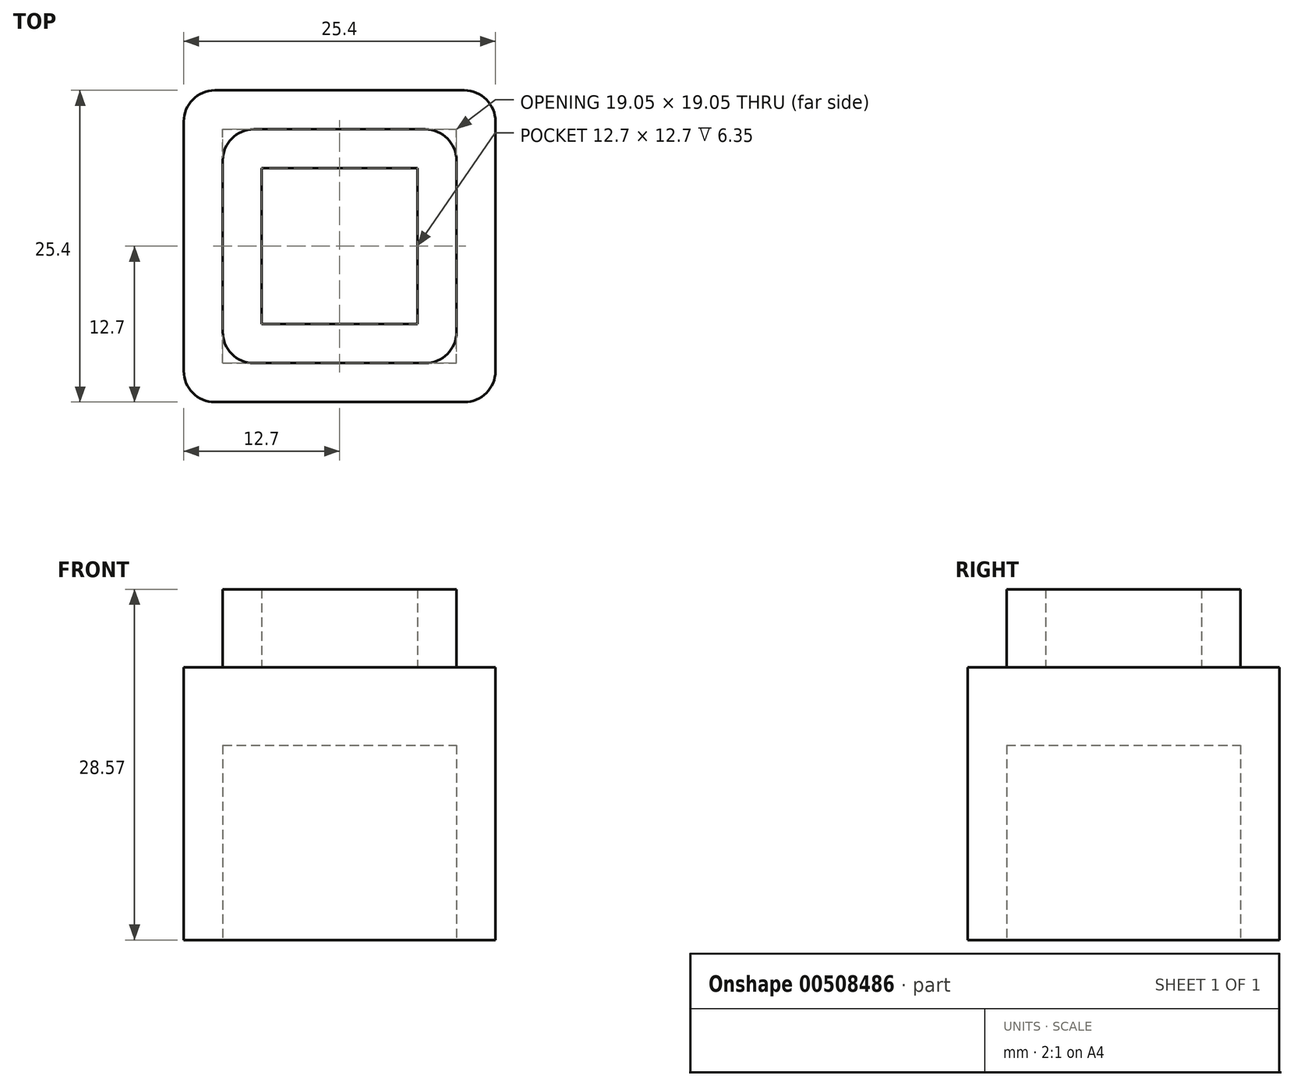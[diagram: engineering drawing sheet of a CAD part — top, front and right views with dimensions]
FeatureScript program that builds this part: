
annotation { "Feature Type Name" : "Feature", "Feature Type Description" : "" }
export const myFeature = defineFeature(function(context is Context, id is Id, definition is map)
    precondition{}
    {
        {
            var Q0;
            Q0=qCreatedBy(makeId("Top.planeOp"),FACE);
            var sketch = newSketch(context, id + "F0", { "sketchPlane" : qUnion([Q0])});
            skLineSegment(sketch, "E0.bottom", {"start": v(0, 0) * mm, "end": v(25.4, 0) * mm});
            skLineSegment(sketch, "E0.top", {"start": v(0, -25.4) * mm, "end": v(25.4, -25.4) * mm});
            skLineSegment(sketch, "E0.left", {"start": v(0, 0) * mm, "end": v(0, -25.4) * mm});
            skLineSegment(sketch, "E0.right", {"start": v(25.4, 0) * mm, "end": v(25.4, -25.4) * mm});
            skSolve(sketch);
        }
        {
            var Q0;
            Q0=qSketchRegion(id+"F0",true);
            extrude(context, id + "F1", {"entities" : qUnion([Q0]), "depth" : 22.22 * mm, "offsetDistance" : 25.4 * mm});
        }
        {
            var Q0;
            Q0=makeQuery(id+"F1.opExtrude","CAP_FACE",FACE,{"disambiguationData":[OSD([sQuery(id+"F0.wireOp",EDGE,"E0.bottom"),sQuery(id+"F0.wireOp",EDGE,"E0.top"),sQuery(id+"F0.wireOp",EDGE,"E0.left"),sQuery(id+"F0.wireOp",EDGE,"E0.right")])],"isStart":true});
            var sketch = newSketch(context, id + "F2", { "sketchPlane" : qUnion([Q0])});
            skLineSegment(sketch, "E1", {"start": v(0, 0) * mm, "end": v(25.4, 25.4) * mm, "construction": true});
            skLineSegment(sketch, "E2.bottom", {"start": v(3.18, 22.23) * mm, "end": v(22.23, 22.23) * mm});
            skLineSegment(sketch, "E2.top", {"start": v(3.18, 3.18) * mm, "end": v(22.23, 3.18) * mm});
            skLineSegment(sketch, "E2.left", {"start": v(3.18, 22.23) * mm, "end": v(3.18, 3.18) * mm});
            skLineSegment(sketch, "E2.right", {"start": v(22.23, 22.23) * mm, "end": v(22.23, 3.18) * mm});
            skLineSegment(sketch, "E3", {"start": v(3.18, 22.23) * mm, "end": v(22.23, 3.18) * mm, "construction": true});
            skPoint(sketch, "E4", {"position": v(12.7, 12.7) * mm});
            skSolve(sketch);
        }
        {
            var Q0;
            Q0=qSketchRegion(id+"F2",true);
            extrude(context, id + "F3", {"entities" : qUnion([Q0]), "operationType" : NewBodyOperationType.REMOVE, "oppositeDirection" : true, "depth" : 15.88 * mm, "offsetDistance" : 25.4 * mm});
        }
        {
            var Q0;
            Q0=makeQuery(id+"F1.opExtrude","CAP_FACE",FACE,{"disambiguationData":[OSD([sQuery(id+"F0.wireOp",EDGE,"E0.bottom"),sQuery(id+"F0.wireOp",EDGE,"E0.top"),sQuery(id+"F0.wireOp",EDGE,"E0.left"),sQuery(id+"F0.wireOp",EDGE,"E0.right")])],"isStart":false});
            var sketch = newSketch(context, id + "F4", { "sketchPlane" : qUnion([Q0])});
            skLineSegment(sketch, "E5.bottom", {"start": v(6.35, -19.05) * mm, "end": v(19.05, -19.05) * mm});
            skLineSegment(sketch, "E5.top", {"start": v(6.35, -6.35) * mm, "end": v(19.05, -6.35) * mm});
            skLineSegment(sketch, "E5.left", {"start": v(6.35, -19.05) * mm, "end": v(6.35, -6.35) * mm});
            skLineSegment(sketch, "E5.right", {"start": v(19.05, -19.05) * mm, "end": v(19.05, -6.35) * mm});
            skLineSegment(sketch, "E6.bottom", {"start": v(3.18, -22.22) * mm, "end": v(22.23, -22.22) * mm});
            skLineSegment(sketch, "E6.top", {"start": v(3.18, -3.17) * mm, "end": v(22.23, -3.17) * mm});
            skLineSegment(sketch, "E6.left", {"start": v(3.18, -22.22) * mm, "end": v(3.18, -3.17) * mm});
            skLineSegment(sketch, "E6.right", {"start": v(22.23, -22.22) * mm, "end": v(22.23, -3.17) * mm});
            skLineSegment(sketch, "E7", {"start": v(0, 0) * mm, "end": v(25.4, -25.4) * mm, "construction": true});
            skLineSegment(sketch, "E8", {"start": v(6.35, -6.35) * mm, "end": v(19.05, -19.05) * mm, "construction": true});
            skLineSegment(sketch, "E9", {"start": v(3.18, -22.22) * mm, "end": v(22.23, -3.17) * mm, "construction": true});
            skPoint(sketch, "E10", {"position": v(12.7, -12.7) * mm});
            skSolve(sketch);
        }
        {
            var Q0;
            Q0=qSketchRegion(id+"F4",true);
            extrude(context, id + "F5", {"entities" : qUnion([Q0]), "operationType" : NewBodyOperationType.ADD, "depth" : 6.35 * mm});
        }
        {
            var Q0;
            Q0=makeQuery(id+"F1.opExtrude","SWEPT_EDGE",EDGE,{"disambiguationData":[OSD([sQuery(id+"F0.wireOp",EDGE,"E0.bottom"),sQuery(id+"F0.wireOp",EDGE,"E0.left")])]});
            var Q1;
            Q1=makeQuery(id+"F1.opExtrude","SWEPT_EDGE",EDGE,{"disambiguationData":[OSD([sQuery(id+"F0.wireOp",EDGE,"E0.top"),sQuery(id+"F0.wireOp",EDGE,"E0.left")])]});
            var Q2;
            Q2=makeQuery(id+"F1.opExtrude","SWEPT_EDGE",EDGE,{"disambiguationData":[OSD([sQuery(id+"F0.wireOp",EDGE,"E0.bottom"),sQuery(id+"F0.wireOp",EDGE,"E0.right")])]});
            var Q3;
            Q3=makeQuery(id+"F5.opExtrude","SWEPT_EDGE",EDGE,{"disambiguationData":[OSD([sQuery(id+"F4.wireOp",EDGE,"E6.top"),sQuery(id+"F4.wireOp",EDGE,"E6.left")])]});
            var Q4;
            Q4=makeQuery(id+"F5.opExtrude","SWEPT_EDGE",EDGE,{"disambiguationData":[OSD([sQuery(id+"F4.wireOp",EDGE,"E6.bottom"),sQuery(id+"F4.wireOp",EDGE,"E6.left")])]});
            var Q5;
            Q5=makeQuery(id+"F5.opExtrude","SWEPT_EDGE",EDGE,{"disambiguationData":[OSD([sQuery(id+"F4.wireOp",EDGE,"E6.top"),sQuery(id+"F4.wireOp",EDGE,"E6.right")])]});
            var Q6;
            Q6=makeQuery(id+"F5.opExtrude","SWEPT_EDGE",EDGE,{"disambiguationData":[OSD([sQuery(id+"F4.wireOp",EDGE,"E6.bottom"),sQuery(id+"F4.wireOp",EDGE,"E6.right")])]});
            var Q7;
            Q7=makeQuery(id+"F1.opExtrude","SWEPT_EDGE",EDGE,{"disambiguationData":[OSD([sQuery(id+"F0.wireOp",EDGE,"E0.top"),sQuery(id+"F0.wireOp",EDGE,"E0.right")])]});
            fillet(context, id + "F6", {"entities" : qUnion([Q0, Q1, Q2, Q3, Q4, Q5, Q6, Q7]), "radius" : 2.54 * mm, "tangentPropagation" : true, "allowEdgeOverflow" : false});
        }
    });
